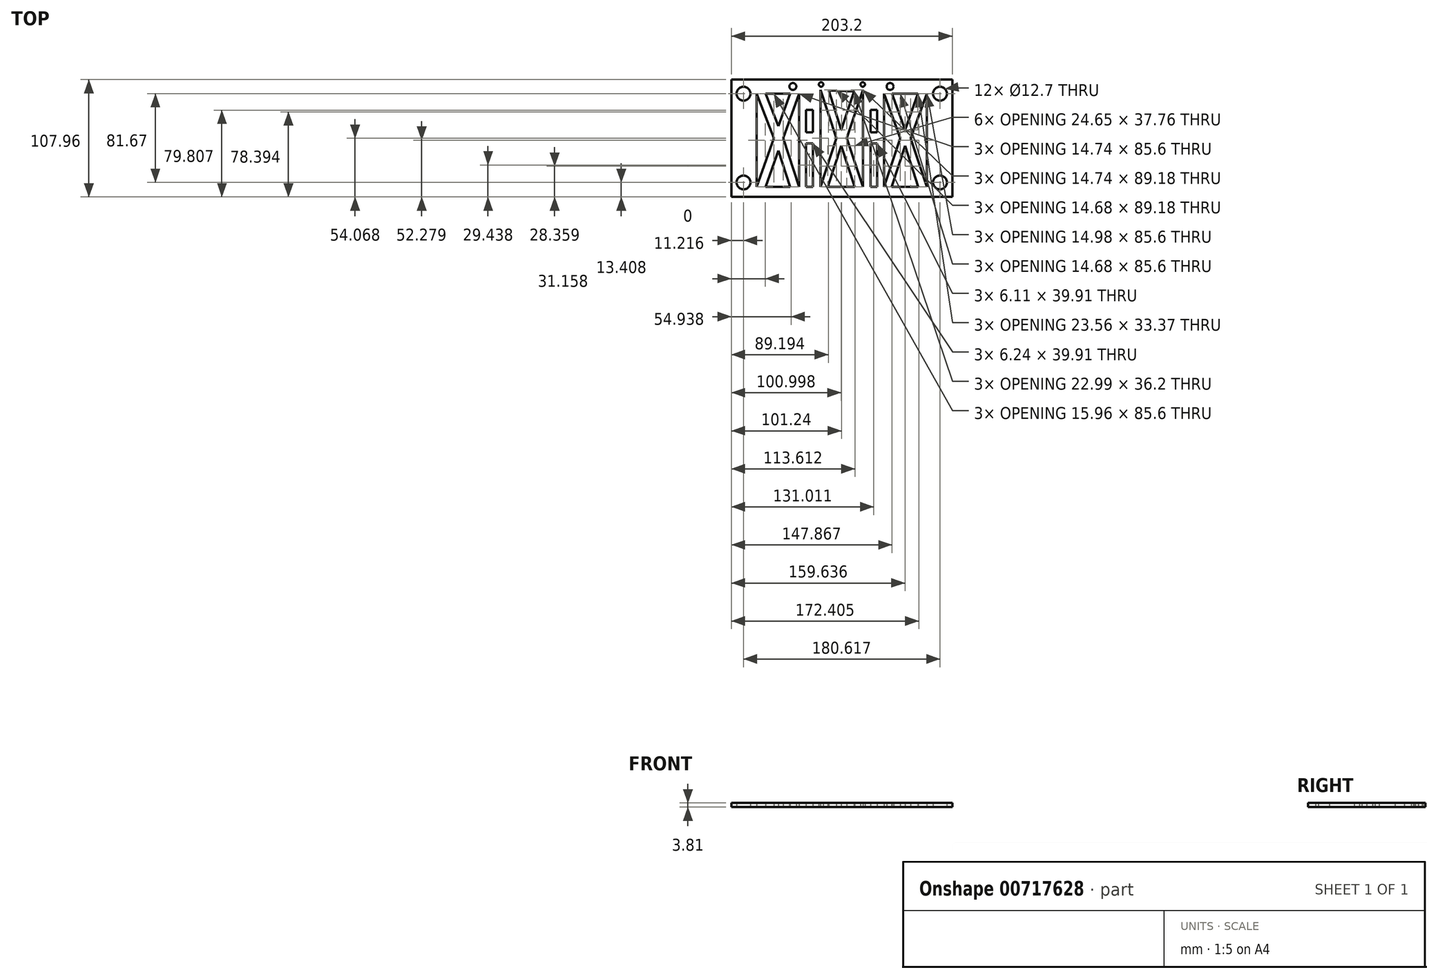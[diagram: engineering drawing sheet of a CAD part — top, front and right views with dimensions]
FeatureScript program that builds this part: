
annotation { "Feature Type Name" : "Feature", "Feature Type Description" : "" }
export const myFeature = defineFeature(function(context is Context, id is Id, definition is map)
    precondition{}
    {
        {
            var Q0;
            Q0=qCreatedBy(makeId("Top.planeOp"),FACE);
            var sketch = newSketch(context, id + "F0", { "sketchPlane" : qUnion([Q0])});
            skLineSegment(sketch, "E0.bottom", {"start": v(-101.6, 53.98) * mm, "end": v(101.6, 53.98) * mm});
            skLineSegment(sketch, "E0.top", {"start": v(-101.6, -53.98) * mm, "end": v(101.6, -53.98) * mm});
            skLineSegment(sketch, "E0.left", {"start": v(-101.6, 53.98) * mm, "end": v(-101.6, -53.98) * mm});
            skLineSegment(sketch, "E0.right", {"start": v(101.6, 53.98) * mm, "end": v(101.6, -53.98) * mm});
            skPoint(sketch, "E0.middle", {"position": v(0, 0) * mm});
            skLineSegment(sketch, "E1", {"start": v(-78.42, 41.1) * mm, "end": v(-78.42, -44.5) * mm});
            skLineSegment(sketch, "E2", {"start": v(-78.42, 41.1) * mm, "end": v(-62.46, 0) * mm});
            skLineSegment(sketch, "E3", {"start": v(-62.46, 0) * mm, "end": v(-78.42, -44.5) * mm});
            skLineSegment(sketch, "E4", {"start": v(-54.03, 0) * mm, "end": v(-39.3, 41.1) * mm});
            skLineSegment(sketch, "E5", {"start": v(-39.3, 41.1) * mm, "end": v(-39.3, -44.5) * mm});
            skLineSegment(sketch, "E6", {"start": v(-39.3, -44.5) * mm, "end": v(-54.03, 0) * mm});
            skLineSegment(sketch, "E7", {"start": v(-69.94, 41.1) * mm, "end": v(-58.36, 11.29) * mm});
            skLineSegment(sketch, "E8", {"start": v(-58.36, 11.29) * mm, "end": v(-47.66, 41.1) * mm});
            skLineSegment(sketch, "E9", {"start": v(-58.36, -11.38) * mm, "end": v(-70.24, -44.5) * mm});
            skLineSegment(sketch, "E10", {"start": v(-70.24, -44.5) * mm, "end": v(-47.66, -44.5) * mm});
            skLineSegment(sketch, "E11", {"start": v(-47.66, -44.5) * mm, "end": v(-58.36, -11.38) * mm});
            skLineSegment(sketch, "E12.1.0.0", {"start": v(11.14, 42.9) * mm, "end": v(-11.86, 43.93) * mm});
            skLineSegment(sketch, "E12.1.0.1", {"start": v(-11.86, 43.93) * mm, "end": v(-0.47, 7.73) * mm});
            skLineSegment(sketch, "E12.1.0.2", {"start": v(-0.47, 7.73) * mm, "end": v(11.14, 42.9) * mm});
            skLineSegment(sketch, "E12.1.0.3", {"start": v(19.38, 44.68) * mm, "end": v(19.38, -44.5) * mm});
            skLineSegment(sketch, "E12.1.0.4", {"start": v(4.64, 0) * mm, "end": v(19.38, 44.68) * mm});
            skLineSegment(sketch, "E12.1.0.5", {"start": v(19.38, -44.5) * mm, "end": v(4.64, 0) * mm});
            skLineSegment(sketch, "E12.1.0.6", {"start": v(11.72, -44.5) * mm, "end": v(-0.47, -6.74) * mm});
            skLineSegment(sketch, "E12.1.0.7", {"start": v(-0.47, -6.74) * mm, "end": v(-12.93, -44.5) * mm});
            skLineSegment(sketch, "E12.1.0.8", {"start": v(-12.93, -44.5) * mm, "end": v(11.72, -44.5) * mm});
            skLineSegment(sketch, "E12.1.0.9", {"start": v(-5.06, 0) * mm, "end": v(-19.75, -44.5) * mm});
            skLineSegment(sketch, "E12.1.0.10", {"start": v(-19.75, 44.68) * mm, "end": v(-19.75, -44.5) * mm});
            skLineSegment(sketch, "E12.1.0.11", {"start": v(-19.75, 44.68) * mm, "end": v(-5.06, 0) * mm});
            skLineSegment(sketch, "E12.2.0.1", {"start": v(46.26, 41.1) * mm, "end": v(58.2, 7.73) * mm});
            skLineSegment(sketch, "E12.2.0.2", {"start": v(58.2, 7.73) * mm, "end": v(69.81, 41.1) * mm});
            skLineSegment(sketch, "E12.2.0.3", {"start": v(78.3, 41.1) * mm, "end": v(78.06, -44.5) * mm});
            skLineSegment(sketch, "E12.2.0.4", {"start": v(63.31, 0) * mm, "end": v(78.3, 41.1) * mm});
            skLineSegment(sketch, "E12.2.0.5", {"start": v(78.06, -44.5) * mm, "end": v(63.31, 0) * mm});
            skLineSegment(sketch, "E12.2.0.6", {"start": v(70.4, -44.5) * mm, "end": v(58.2, -6.74) * mm});
            skLineSegment(sketch, "E12.2.0.7", {"start": v(58.2, -6.74) * mm, "end": v(45.75, -44.5) * mm});
            skLineSegment(sketch, "E12.2.0.8", {"start": v(45.75, -44.5) * mm, "end": v(70.4, -44.5) * mm});
            skLineSegment(sketch, "E12.2.0.9", {"start": v(53.6, 0) * mm, "end": v(38.93, -44.5) * mm});
            skLineSegment(sketch, "E12.2.0.10", {"start": v(38.93, 41.1) * mm, "end": v(38.93, -44.5) * mm});
            skLineSegment(sketch, "E12.2.0.11", {"start": v(38.93, 41.1) * mm, "end": v(53.6, 0) * mm});
            skLineSegment(sketch, "E13.top", {"start": v(-32.83, 5.48) * mm, "end": v(-26.58, 5.48) * mm});
            skLineSegment(sketch, "E14.bottom", {"start": v(-32.83, -4.58) * mm, "end": v(-26.58, -4.58) * mm});
            skLineSegment(sketch, "E14.top", {"start": v(-32.83, -44.5) * mm, "end": v(-26.58, -44.5) * mm});
            skLineSegment(sketch, "E14.left", {"start": v(-32.83, -4.58) * mm, "end": v(-32.83, -44.5) * mm});
            skLineSegment(sketch, "E14.right", {"start": v(-26.58, -4.58) * mm, "end": v(-26.58, -44.5) * mm});
            skLineSegment(sketch, "E15.1.0.3", {"start": v(26.36, 5.48) * mm, "end": v(32.47, 5.48) * mm});
            skLineSegment(sketch, "E15.1.0.4", {"start": v(26.36, -4.58) * mm, "end": v(32.47, -4.58) * mm});
            skLineSegment(sketch, "E15.1.0.5", {"start": v(26.36, -4.58) * mm, "end": v(26.36, -44.5) * mm});
            skLineSegment(sketch, "E15.1.0.6", {"start": v(26.36, -44.5) * mm, "end": v(32.47, -44.5) * mm});
            skLineSegment(sketch, "E15.1.0.7", {"start": v(32.47, -4.58) * mm, "end": v(32.47, -44.5) * mm});
            skCircle(sketch, "E16", {"center": v(-19.08, 49.58) * mm, "radius": 2.03 * mm});
            skCircle(sketch, "E17", {"center": v(19.23, 49.58) * mm, "radius": 2.03 * mm});
            skLineSegment(sketch, "E18", {"start": v(-32.83, 5.48) * mm, "end": v(-32.83, 26.2) * mm});
            skPoint(sketch, "E18.endSnap0", {"position": v(-53.01, 26.2) * mm});
            skLineSegment(sketch, "E19", {"start": v(-32.83, 26.2) * mm, "end": v(-26.58, 26.2) * mm});
            skLineSegment(sketch, "E20", {"start": v(-26.58, 26.2) * mm, "end": v(-26.58, 5.48) * mm});
            skLineSegment(sketch, "E21", {"start": v(26.36, 5.48) * mm, "end": v(26.36, 26.2) * mm});
            skLineSegment(sketch, "E22", {"start": v(26.36, 26.2) * mm, "end": v(32.47, 26.2) * mm});
            skLineSegment(sketch, "E23", {"start": v(32.47, 26.2) * mm, "end": v(32.47, 5.48) * mm});
            skCircle(sketch, "E24", {"center": v(-45.03, 47.7) * mm, "radius": 3.18 * mm});
            skCircle(sketch, "E25", {"center": v(44.37, 47.7) * mm, "radius": 3.18 * mm});
            skLineSegment(sketch, "E26", {"start": v(-47.66, 41.1) * mm, "end": v(-69.94, 41.1) * mm});
            skLineSegment(sketch, "E27", {"start": v(46.26, 41.1) * mm, "end": v(69.81, 41.1) * mm});
            skCircle(sketch, "E28", {"center": v(-90.38, 41.1) * mm, "radius": 6.35 * mm});
            skCircle(sketch, "E29", {"center": v(-90.38, -40.57) * mm, "radius": 6.35 * mm});
            skCircle(sketch, "E30", {"center": v(90.23, -40.57) * mm, "radius": 6.35 * mm});
            skCircle(sketch, "E31", {"center": v(90.23, 41.1) * mm, "radius": 6.35 * mm});
            skPoint(sketch, "E32", {"position": v(58.04, 41.1) * mm});
            skSolve(sketch);
        }
        {
            var Q0;
            Q0=qSketchRegion(id+"F0",true);
            extrude(context, id + "F1", {"entities" : qUnion([Q0]), "depth" : 3.8 * mm, "offsetDistance" : 25.4 * mm});
        }
    });
